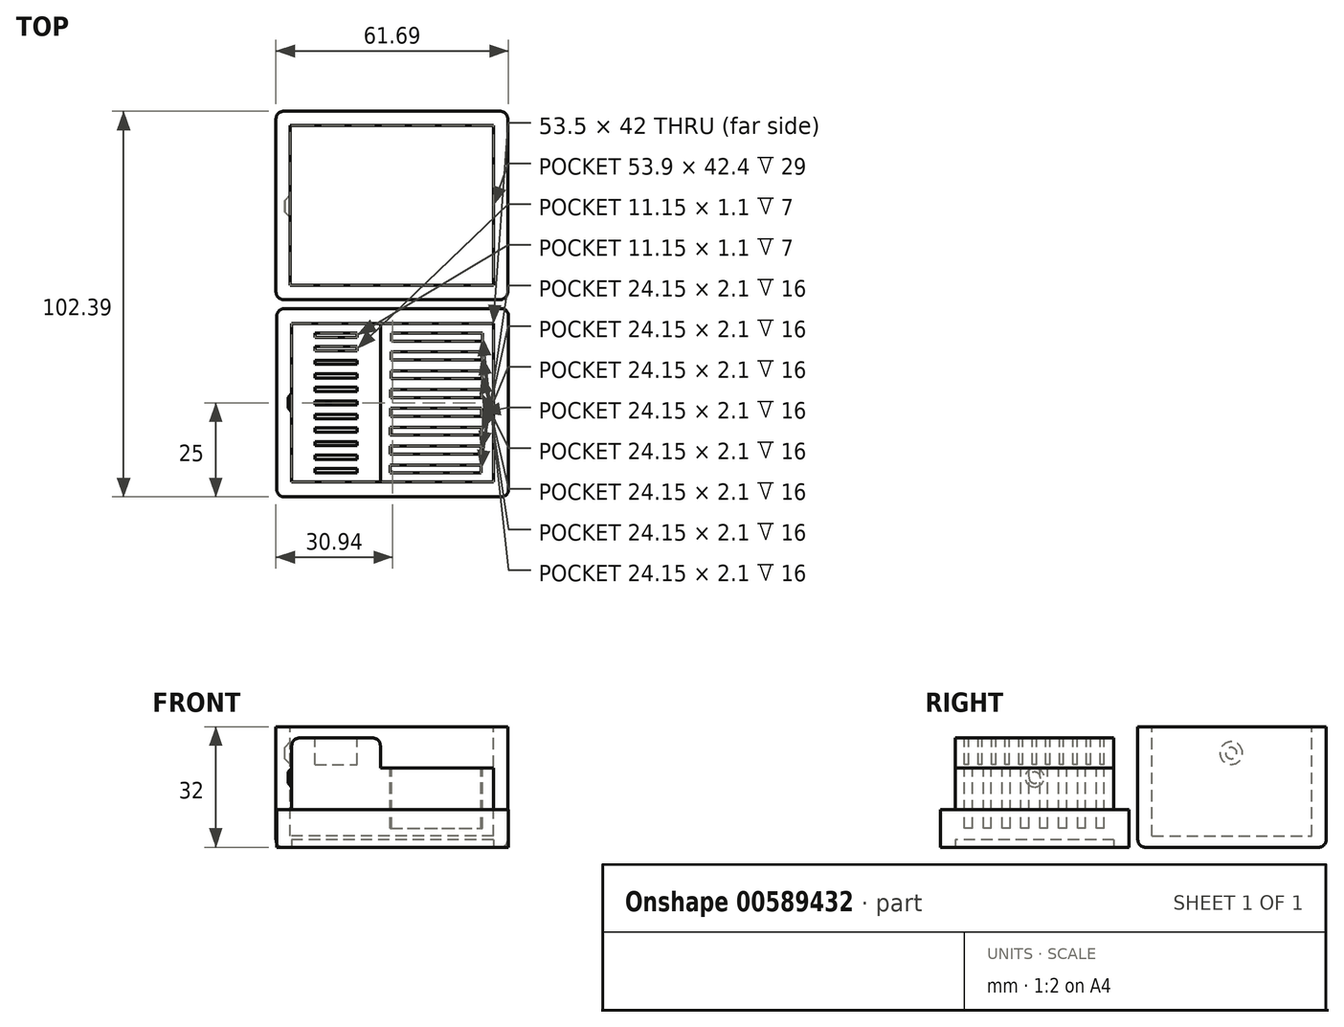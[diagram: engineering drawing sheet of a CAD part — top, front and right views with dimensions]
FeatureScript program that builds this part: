
annotation { "Feature Type Name" : "Feature", "Feature Type Description" : "" }
export const myFeature = defineFeature(function(context is Context, id is Id, definition is map)
    precondition{}
    {
        {
            var Q0;
            Q0=qCreatedBy(makeId("Top.planeOp"),FACE);
            var sketch = newSketch(context, id + "F0", { "sketchPlane" : qUnion([Q0])});
            skLineSegment(sketch, "E0.bottom", {"start": v(30.75, -25) * mm, "end": v(-30.75, -25) * mm});
            skLineSegment(sketch, "E0.top", {"start": v(30.75, 25) * mm, "end": v(-30.75, 25) * mm});
            skLineSegment(sketch, "E0.left", {"start": v(30.75, -25) * mm, "end": v(30.75, 25) * mm});
            skLineSegment(sketch, "E0.right", {"start": v(-30.75, -25) * mm, "end": v(-30.75, 25) * mm});
            skPoint(sketch, "E0.middle", {"position": v(0, 0) * mm});
            skSolve(sketch);
        }
        {
            var Q0;
            Q0=qSketchRegion(id+"F0",true);
            extrude(context, id + "F1", {"entities" : qUnion([Q0]), "depth" : 21 * mm, "offsetDistance" : 25 * mm});
        }
        {
            var Q0;
            Q0=makeQuery(id+"F1.opExtrude","CAP_FACE",FACE,{"disambiguationData":[OSD([sQuery(id+"F0.wireOp",EDGE,"E0.bottom"),sQuery(id+"F0.wireOp",EDGE,"E0.top"),sQuery(id+"F0.wireOp",EDGE,"E0.left"),sQuery(id+"F0.wireOp",EDGE,"E0.right")])],"isStart":false});
            var sketch = newSketch(context, id + "F2", { "sketchPlane" : qUnion([Q0])});
            skLineSegment(sketch, "E1.bottom", {"start": v(26.75, -21) * mm, "end": v(-26.75, -21) * mm});
            skLineSegment(sketch, "E1.top", {"start": v(26.75, 21) * mm, "end": v(-26.75, 21) * mm});
            skLineSegment(sketch, "E1.left", {"start": v(26.75, -21) * mm, "end": v(26.75, 21) * mm});
            skLineSegment(sketch, "E1.right", {"start": v(-26.75, -21) * mm, "end": v(-26.75, 21) * mm});
            skPoint(sketch, "E1.middle", {"position": v(0, 0) * mm});
            skSolve(sketch);
        }
        {
            var Q0;
            Q0=makeQuery(id+"F2.imprint","IMPRINT",FACE,{"disambiguationData":[TD([[makeQuery(id+"F2.imprint","IMPRINT",EDGE,{"derivedFrom":sQuery(id+"F2.wireOp",EDGE,"E1.bottom")}),1.0]])]});
            extrude(context, id + "F3", {"entities" : qUnion([Q0]), "operationType" : NewBodyOperationType.REMOVE, "oppositeDirection" : true, "depth" : 11 * mm, "offsetDistance" : 25 * mm});
        }
        {
            var Q0;
            Q0=makeQuery(id+"F1.opExtrude","CAP_FACE",FACE,{"disambiguationData":[OSD([sQuery(id+"F0.wireOp",EDGE,"E0.bottom"),sQuery(id+"F0.wireOp",EDGE,"E0.top"),sQuery(id+"F0.wireOp",EDGE,"E0.left"),sQuery(id+"F0.wireOp",EDGE,"E0.right")])],"isStart":false});
            var sketch = newSketch(context, id + "F4", { "sketchPlane" : qUnion([Q0])});
            skLineSegment(sketch, "E2.bottom", {"start": v(0, 21) * mm, "end": v(-26.75, 21) * mm});
            skLineSegment(sketch, "E2.top", {"start": v(0, -21) * mm, "end": v(-26.75, -21) * mm});
            skLineSegment(sketch, "E2.right", {"start": v(-26.75, 21) * mm, "end": v(-26.75, -21) * mm});
            skLineSegment(sketch, "E3.bottom", {"start": v(-26.75, 21) * mm, "end": v(-3.25, 21) * mm});
            skLineSegment(sketch, "E3.top", {"start": v(-26.75, -21) * mm, "end": v(-3.25, -21) * mm});
            skLineSegment(sketch, "E3.right", {"start": v(-3.25, 21) * mm, "end": v(-3.25, -21) * mm});
            skSolve(sketch);
        }
        {
            var Q0;
            Q0=qSketchRegion(id+"F4",true);
            extrude(context, id + "F5", {"entities" : qUnion([Q0]), "operationType" : NewBodyOperationType.ADD, "depth" : 8 * mm, "offsetDistance" : 25 * mm});
        }
        {
            var Q0;
            Q0=makeQuery(id+"F5.opExtrude","CAP_FACE",FACE,{"disambiguationData":[OSD([sQuery(id+"F4.wireOp",EDGE,"E3.bottom"),sQuery(id+"F4.wireOp",EDGE,"E3.top"),sQuery(id+"F4.wireOp",EDGE,"E2.right"),sQuery(id+"F4.wireOp",EDGE,"E3.right")])],"isStart":false});
            var sketch = newSketch(context, id + "F6", { "sketchPlane" : qUnion([Q0])});
            skLineSegment(sketch, "E4.bottom", {"start": v(-20.57, 18.5) * mm, "end": v(-9.42, 18.5) * mm});
            skLineSegment(sketch, "E4.top", {"start": v(-20.57, 17.4) * mm, "end": v(-9.42, 17.4) * mm});
            skLineSegment(sketch, "E4.left", {"start": v(-20.57, 18.5) * mm, "end": v(-20.57, 17.4) * mm});
            skLineSegment(sketch, "E4.right", {"start": v(-9.42, 18.5) * mm, "end": v(-9.42, 17.4) * mm});
            skLineSegment(sketch, "E5.1.0.0", {"start": v(-20.57, 14.9) * mm, "end": v(-9.42, 14.9) * mm});
            skLineSegment(sketch, "E5.1.0.1", {"start": v(-20.57, 13.8) * mm, "end": v(-9.42, 13.8) * mm});
            skLineSegment(sketch, "E5.1.0.2", {"start": v(-9.42, 14.9) * mm, "end": v(-9.42, 13.8) * mm});
            skLineSegment(sketch, "E5.1.0.3", {"start": v(-20.57, 14.9) * mm, "end": v(-20.57, 13.8) * mm});
            skLineSegment(sketch, "E5.2.0.0", {"start": v(-20.57, 11.3) * mm, "end": v(-9.42, 11.3) * mm});
            skLineSegment(sketch, "E5.2.0.1", {"start": v(-20.57, 10.2) * mm, "end": v(-9.42, 10.2) * mm});
            skLineSegment(sketch, "E5.2.0.2", {"start": v(-9.42, 11.3) * mm, "end": v(-9.42, 10.2) * mm});
            skLineSegment(sketch, "E5.2.0.3", {"start": v(-20.57, 11.3) * mm, "end": v(-20.57, 10.2) * mm});
            skLineSegment(sketch, "E5.3.0.0", {"start": v(-20.57, 7.7) * mm, "end": v(-9.42, 7.7) * mm});
            skLineSegment(sketch, "E5.3.0.1", {"start": v(-20.57, 6.6) * mm, "end": v(-9.42, 6.6) * mm});
            skLineSegment(sketch, "E5.3.0.2", {"start": v(-9.42, 7.7) * mm, "end": v(-9.42, 6.6) * mm});
            skLineSegment(sketch, "E5.3.0.3", {"start": v(-20.57, 7.7) * mm, "end": v(-20.57, 6.6) * mm});
            skLineSegment(sketch, "E5.4.0.0", {"start": v(-20.57, 4.1) * mm, "end": v(-9.42, 4.1) * mm});
            skLineSegment(sketch, "E5.4.0.1", {"start": v(-20.57, 3) * mm, "end": v(-9.42, 3) * mm});
            skLineSegment(sketch, "E5.4.0.2", {"start": v(-9.42, 4.1) * mm, "end": v(-9.42, 3) * mm});
            skLineSegment(sketch, "E5.4.0.3", {"start": v(-20.57, 4.1) * mm, "end": v(-20.57, 3) * mm});
            skLineSegment(sketch, "E5.5.0.0", {"start": v(-20.57, 0.5) * mm, "end": v(-9.42, 0.5) * mm});
            skLineSegment(sketch, "E5.5.0.1", {"start": v(-20.57, -0.6) * mm, "end": v(-9.42, -0.6) * mm});
            skLineSegment(sketch, "E5.5.0.2", {"start": v(-9.42, 0.5) * mm, "end": v(-9.42, -0.6) * mm});
            skLineSegment(sketch, "E5.5.0.3", {"start": v(-20.57, 0.5) * mm, "end": v(-20.57, -0.6) * mm});
            skLineSegment(sketch, "E5.6.0.0", {"start": v(-20.57, -3.1) * mm, "end": v(-9.42, -3.1) * mm});
            skLineSegment(sketch, "E5.6.0.1", {"start": v(-20.57, -4.2) * mm, "end": v(-9.42, -4.2) * mm});
            skLineSegment(sketch, "E5.6.0.2", {"start": v(-9.42, -3.1) * mm, "end": v(-9.42, -4.2) * mm});
            skLineSegment(sketch, "E5.6.0.3", {"start": v(-20.57, -3.1) * mm, "end": v(-20.57, -4.2) * mm});
            skLineSegment(sketch, "E5.7.0.0", {"start": v(-20.57, -6.7) * mm, "end": v(-9.42, -6.7) * mm});
            skLineSegment(sketch, "E5.7.0.1", {"start": v(-20.57, -7.8) * mm, "end": v(-9.42, -7.8) * mm});
            skLineSegment(sketch, "E5.7.0.2", {"start": v(-9.42, -6.7) * mm, "end": v(-9.42, -7.8) * mm});
            skLineSegment(sketch, "E5.7.0.3", {"start": v(-20.57, -6.7) * mm, "end": v(-20.57, -7.8) * mm});
            skLineSegment(sketch, "E5.8.0.0", {"start": v(-20.57, -10.3) * mm, "end": v(-9.42, -10.3) * mm});
            skLineSegment(sketch, "E5.8.0.1", {"start": v(-20.57, -11.4) * mm, "end": v(-9.42, -11.4) * mm});
            skLineSegment(sketch, "E5.8.0.2", {"start": v(-9.42, -10.3) * mm, "end": v(-9.42, -11.4) * mm});
            skLineSegment(sketch, "E5.8.0.3", {"start": v(-20.57, -10.3) * mm, "end": v(-20.57, -11.4) * mm});
            skLineSegment(sketch, "E5.9.0.0", {"start": v(-20.57, -13.9) * mm, "end": v(-9.42, -13.9) * mm});
            skLineSegment(sketch, "E5.9.0.1", {"start": v(-20.57, -15) * mm, "end": v(-9.42, -15) * mm});
            skLineSegment(sketch, "E5.9.0.2", {"start": v(-9.42, -13.9) * mm, "end": v(-9.42, -15) * mm});
            skLineSegment(sketch, "E5.9.0.3", {"start": v(-20.57, -13.9) * mm, "end": v(-20.57, -15) * mm});
            skLineSegment(sketch, "E5.10.0.0", {"start": v(-20.57, -17.5) * mm, "end": v(-9.42, -17.5) * mm});
            skLineSegment(sketch, "E5.10.0.1", {"start": v(-20.57, -18.6) * mm, "end": v(-9.42, -18.6) * mm});
            skLineSegment(sketch, "E5.10.0.2", {"start": v(-9.42, -17.5) * mm, "end": v(-9.42, -18.6) * mm});
            skLineSegment(sketch, "E5.10.0.3", {"start": v(-20.57, -17.5) * mm, "end": v(-20.57, -18.6) * mm});
            skLineSegment(sketch, "E5.direction1", {"start": v(-17.32, 17.5) * mm, "end": v(-17.32, 13.9) * mm, "construction": true});
            skSolve(sketch);
        }
        {
            var Q0;
            Q0=qSketchRegion(id+"F6",true);
            extrude(context, id + "F7", {"entities" : qUnion([Q0]), "operationType" : NewBodyOperationType.REMOVE, "oppositeDirection" : true, "depth" : 7 * mm, "offsetDistance" : 25 * mm});
        }
        {
            var Q0;
            Q0=makeQuery(id+"F1.opExtrude","CAP_FACE",FACE,{"disambiguationData":[OSD([sQuery(id+"F0.wireOp",EDGE,"E0.bottom"),sQuery(id+"F0.wireOp",EDGE,"E0.top"),sQuery(id+"F0.wireOp",EDGE,"E0.left"),sQuery(id+"F0.wireOp",EDGE,"E0.right")])],"isStart":false});
            var sketch = newSketch(context, id + "F8", { "sketchPlane" : qUnion([Q0])});
            skLineSegment(sketch, "E6.bottom", {"start": v(-0.33, 18.5) * mm, "end": v(23.82, 18.5) * mm});
            skLineSegment(sketch, "E6.top", {"start": v(-0.33, 16.4) * mm, "end": v(23.82, 16.4) * mm});
            skLineSegment(sketch, "E6.left", {"start": v(-0.33, 18.5) * mm, "end": v(-0.33, 16.4) * mm});
            skLineSegment(sketch, "E6.right", {"start": v(23.82, 18.5) * mm, "end": v(23.82, 16.4) * mm});
            skLineSegment(sketch, "E7.1.0.0", {"start": v(-0.38, 11.4) * mm, "end": v(23.77, 11.4) * mm});
            skLineSegment(sketch, "E7.1.0.1", {"start": v(23.77, 13.5) * mm, "end": v(23.77, 11.4) * mm});
            skLineSegment(sketch, "E7.1.0.2", {"start": v(-0.38, 13.5) * mm, "end": v(-0.38, 11.4) * mm});
            skLineSegment(sketch, "E7.1.0.3", {"start": v(-0.38, 13.5) * mm, "end": v(23.77, 13.5) * mm});
            skLineSegment(sketch, "E7.2.0.0", {"start": v(-0.44, 6.4) * mm, "end": v(23.71, 6.4) * mm});
            skLineSegment(sketch, "E7.2.0.1", {"start": v(23.71, 8.5) * mm, "end": v(23.71, 6.4) * mm});
            skLineSegment(sketch, "E7.2.0.2", {"start": v(-0.44, 8.5) * mm, "end": v(-0.44, 6.4) * mm});
            skLineSegment(sketch, "E7.2.0.3", {"start": v(-0.44, 8.5) * mm, "end": v(23.71, 8.5) * mm});
            skLineSegment(sketch, "E7.direction1", {"start": v(-0.33, 16.4) * mm, "end": v(-0.38, 11.4) * mm, "construction": true});
            skLineSegment(sketch, "E8.0.3.0", {"start": v(-0.5, 1.4) * mm, "end": v(23.66, 1.4) * mm});
            skLineSegment(sketch, "E8.3.3.0", {"start": v(23.66, 3.5) * mm, "end": v(23.66, 1.4) * mm});
            skLineSegment(sketch, "E8.6.3.0", {"start": v(-0.5, 3.5) * mm, "end": v(-0.5, 1.4) * mm});
            skLineSegment(sketch, "E8.9.3.0", {"start": v(-0.5, 3.5) * mm, "end": v(23.66, 3.5) * mm});
            skLineSegment(sketch, "E8.0.4.0", {"start": v(-0.55, -3.6) * mm, "end": v(23.6, -3.6) * mm});
            skLineSegment(sketch, "E8.3.4.0", {"start": v(23.6, -1.5) * mm, "end": v(23.6, -3.6) * mm});
            skLineSegment(sketch, "E8.6.4.0", {"start": v(-0.55, -1.5) * mm, "end": v(-0.55, -3.6) * mm});
            skLineSegment(sketch, "E8.9.4.0", {"start": v(-0.55, -1.5) * mm, "end": v(23.6, -1.5) * mm});
            skLineSegment(sketch, "E8.0.5.0", {"start": v(-0.6, -8.6) * mm, "end": v(23.55, -8.6) * mm});
            skLineSegment(sketch, "E8.3.5.0", {"start": v(23.55, -6.5) * mm, "end": v(23.55, -8.6) * mm});
            skLineSegment(sketch, "E8.6.5.0", {"start": v(-0.6, -6.5) * mm, "end": v(-0.6, -8.6) * mm});
            skLineSegment(sketch, "E8.9.5.0", {"start": v(-0.6, -6.5) * mm, "end": v(23.55, -6.5) * mm});
            skLineSegment(sketch, "E9.0.6.0", {"start": v(-0.66, -13.6) * mm, "end": v(23.5, -13.6) * mm});
            skLineSegment(sketch, "E9.3.6.0", {"start": v(23.5, -11.5) * mm, "end": v(23.5, -13.6) * mm});
            skLineSegment(sketch, "E9.6.6.0", {"start": v(-0.66, -11.5) * mm, "end": v(-0.66, -13.6) * mm});
            skLineSegment(sketch, "E9.9.6.0", {"start": v(-0.66, -11.5) * mm, "end": v(23.5, -11.5) * mm});
            skLineSegment(sketch, "E10.0.7.0", {"start": v(-0.71, -18.6) * mm, "end": v(23.44, -18.6) * mm});
            skLineSegment(sketch, "E10.3.7.0", {"start": v(23.44, -16.5) * mm, "end": v(23.44, -18.6) * mm});
            skLineSegment(sketch, "E10.6.7.0", {"start": v(-0.71, -16.5) * mm, "end": v(-0.71, -18.6) * mm});
            skLineSegment(sketch, "E10.9.7.0", {"start": v(-0.71, -16.5) * mm, "end": v(23.44, -16.5) * mm});
            skSolve(sketch);
        }
        {
            var Q0;
            Q0=qSketchRegion(id+"F8",true);
            extrude(context, id + "F9", {"entities" : qUnion([Q0]), "operationType" : NewBodyOperationType.REMOVE, "oppositeDirection" : true, "depth" : 16 * mm, "offsetDistance" : 25 * mm});
        }
        {
            var Q0;
            Q0=makeQuery(id+"F5.opExtrude","CAP_EDGE",EDGE,{"disambiguationData":[OSD([sQuery(id+"F4.wireOp",EDGE,"E3.right")])],"isStart":false});
            var Q1;
            Q1=makeQuery(id+"F3.boolean.opBoolean","COPY",EDGE,{"derivedFrom":makeQuery(id+"F3.opExtrude","CAP_EDGE",EDGE,{"disambiguationData":[OSD([sQuery(id+"F2.wireOp",EDGE,"E1.left")])],"isStart":true})});
            var Q2;
            Q2=makeQuery(id+"F5.opExtrude","CAP_EDGE",EDGE,{"disambiguationData":[OSD([sQuery(id+"F4.wireOp",EDGE,"E2.right")])],"isStart":false});
            var Q3;
            Q3=makeQuery(id+"F5.opExtrude","CAP_EDGE",EDGE,{"disambiguationData":[OSD([sQuery(id+"F4.wireOp",EDGE,"E3.right")])],"isStart":true});
            var Q4;
            Q4=makeQuery(id+"F1.opExtrude","SWEPT_EDGE",EDGE,{"disambiguationData":[OSD([sQuery(id+"F0.wireOp",EDGE,"E0.bottom"),sQuery(id+"F0.wireOp",EDGE,"E0.right")])]});
            var Q5;
            Q5=makeQuery(id+"F1.opExtrude","SWEPT_EDGE",EDGE,{"disambiguationData":[OSD([sQuery(id+"F0.wireOp",EDGE,"E0.top"),sQuery(id+"F0.wireOp",EDGE,"E0.right")])]});
            var Q6;
            Q6=makeQuery(id+"F1.opExtrude","SWEPT_EDGE",EDGE,{"disambiguationData":[OSD([sQuery(id+"F0.wireOp",EDGE,"E0.bottom"),sQuery(id+"F0.wireOp",EDGE,"E0.left")])]});
            var Q7;
            Q7=makeQuery(id+"F1.opExtrude","SWEPT_EDGE",EDGE,{"disambiguationData":[OSD([sQuery(id+"F0.wireOp",EDGE,"E0.top"),sQuery(id+"F0.wireOp",EDGE,"E0.left")])]});
            var Q8;
            Q8=makeQuery(id+"F5.opExtrude","CAP_EDGE",EDGE,{"disambiguationData":[OSD([sQuery(id+"F4.wireOp",EDGE,"E3.top")])],"isStart":false});
            var Q9;
            Q9=makeQuery(id+"F3.boolean.opBoolean","COPY",EDGE,{"derivedFrom":makeQuery(id+"F3.opExtrude","CAP_EDGE",EDGE,{"disambiguationData":[OSD([sQuery(id+"F2.wireOp",EDGE,"E1.bottom")])],"isStart":true})});
            var Q10;
            Q10=makeQuery(id+"F3.boolean.opBoolean","COPY",EDGE,{"derivedFrom":makeQuery(id+"F3.opExtrude","CAP_EDGE",EDGE,{"disambiguationData":[OSD([sQuery(id+"F2.wireOp",EDGE,"E1.top")])],"isStart":true})});
            var Q11;
            Q11=makeQuery(id+"F5.opExtrude","CAP_EDGE",EDGE,{"disambiguationData":[OSD([sQuery(id+"F4.wireOp",EDGE,"E3.bottom")])],"isStart":false});
            fillet(context, id + "F10", {"entities" : qUnion([Q0, Q1, Q2, Q3, Q4, Q5, Q6, Q7, Q8, Q9, Q10, Q11]), "radius" : 2 * mm, "tangentPropagation" : true, "allowEdgeOverflow" : false});
        }
        {
            var Q0;
            Q0=qCreatedBy(makeId("Top.planeOp"),FACE);
            var sketch = newSketch(context, id + "F11", { "sketchPlane" : qUnion([Q0])});
            skLineSegment(sketch, "E11.bottom", {"start": v(-30.94, 77.39) * mm, "end": v(30.56, 77.39) * mm});
            skLineSegment(sketch, "E11.top", {"start": v(-30.94, 27.39) * mm, "end": v(30.56, 27.39) * mm});
            skLineSegment(sketch, "E11.left", {"start": v(-30.94, 77.39) * mm, "end": v(-30.94, 27.39) * mm});
            skLineSegment(sketch, "E11.right", {"start": v(30.56, 77.39) * mm, "end": v(30.56, 27.39) * mm});
            skSolve(sketch);
        }
        {
            var Q0;
            Q0=qSketchRegion(id+"F11",true);
            extrude(context, id + "F12", {"entities" : qUnion([Q0]), "depth" : 32 * mm, "offsetDistance" : 25 * mm});
        }
        {
            var Q0;
            Q0=makeQuery(id+"F12.opExtrude","CAP_FACE",FACE,{"disambiguationData":[OSD([sQuery(id+"F11.wireOp",EDGE,"E11.bottom"),sQuery(id+"F11.wireOp",EDGE,"E11.top"),sQuery(id+"F11.wireOp",EDGE,"E11.left"),sQuery(id+"F11.wireOp",EDGE,"E11.right")])],"isStart":false});
            var sketch = newSketch(context, id + "F13", { "sketchPlane" : qUnion([Q0])});
            skLineSegment(sketch, "E12.bottom", {"start": v(26.76, 31.19) * mm, "end": v(-27.14, 31.19) * mm});
            skLineSegment(sketch, "E12.top", {"start": v(26.76, 73.59) * mm, "end": v(-27.14, 73.59) * mm});
            skLineSegment(sketch, "E12.left", {"start": v(26.76, 31.19) * mm, "end": v(26.76, 73.59) * mm});
            skLineSegment(sketch, "E12.right", {"start": v(-27.14, 31.19) * mm, "end": v(-27.14, 73.59) * mm});
            skPoint(sketch, "E12.middle", {"position": v(-0.2, 52.39) * mm});
            skPoint(sketch, "E12.middle.positionSnap0", {"position": v(-30.94, 52.39) * mm});
            skPoint(sketch, "E12.middle.positionSnap1", {"position": v(-0.2, 77.39) * mm});
            skPoint(sketch, "E12.centerSnap0", {"position": v(-30.94, 52.39) * mm});
            skPoint(sketch, "E12.centerSnap1", {"position": v(-0.2, 77.39) * mm});
            skSolve(sketch);
        }
        {
            var Q0;
            Q0=qSketchRegion(id+"F13",true);
            extrude(context, id + "F14", {"entities" : qUnion([Q0]), "operationType" : NewBodyOperationType.REMOVE, "oppositeDirection" : true, "depth" : 29 * mm, "offsetDistance" : 25 * mm});
        }
        {
            var Q0;
            Q0=makeQuery(id+"F5.boolean.opBoolean","MERGE",FACE,{"derivedFrom":[makeQuery(id+"F3.boolean.opBoolean","COPY",FACE,{"derivedFrom":makeQuery(id+"F3.opExtrude","SWEPT_FACE",FACE,{"disambiguationData":[OSD([sQuery(id+"F2.wireOp",EDGE,"E1.right")])]})}),makeQuery(id+"F5.opExtrude","SWEPT_FACE",FACE,{"disambiguationData":[OSD([sQuery(id+"F4.wireOp",EDGE,"E2.right")])]})]});
            var sketch = newSketch(context, id + "F15", { "sketchPlane" : qUnion([Q0])});
            skCircle(sketch, "E13", {"center": v(0, 18.5) * mm, "radius": 2.5 * mm});
            skPoint(sketch, "E13.centerSnap0", {"position": v(-21, 18.5) * mm});
            skPoint(sketch, "E13.centerSnap1", {"position": v(0, 27) * mm});
            skSolve(sketch);
        }
        {
            var Q0;
            Q0=qSketchRegion(id+"F15",true);
            extrude(context, id + "F16", {"entities" : qUnion([Q0]), "operationType" : NewBodyOperationType.ADD, "depth" : 1 * mm, "offsetDistance" : 25 * mm, "hasDraft" : true, "draftAngle" : 45 * degree, "draftPullDirection" : true});
        }
        {
            var Q0;
            Q0=makeQuery(id+"F14.boolean.opBoolean","COPY",FACE,{"derivedFrom":makeQuery(id+"F14.opExtrude","SWEPT_FACE",FACE,{"disambiguationData":[OSD([sQuery(id+"F13.wireOp",EDGE,"E12.right")])]})});
            var sketch = newSketch(context, id + "F17", { "sketchPlane" : qUnion([Q0])});
            skCircle(sketch, "E14", {"center": v(52.19, 25) * mm, "radius": 3 * mm});
            skSolve(sketch);
        }
        {
            var Q0;
            Q0=qSketchRegion(id+"F17",true);
            extrude(context, id + "F18", {"entities" : qUnion([Q0]), "operationType" : NewBodyOperationType.REMOVE, "oppositeDirection" : true, "depth" : 1.5 * mm, "offsetDistance" : 25 * mm, "hasDraft" : true, "draftAngle" : 45 * degree, "draftPullDirection" : true});
        }
        {
            var Q0;
            Q0=makeQuery(id+"F12.opExtrude","CAP_FACE",FACE,{"disambiguationData":[OSD([sQuery(id+"F11.wireOp",EDGE,"E11.bottom"),sQuery(id+"F11.wireOp",EDGE,"E11.top"),sQuery(id+"F11.wireOp",EDGE,"E11.left"),sQuery(id+"F11.wireOp",EDGE,"E11.right")])],"isStart":true});
            var Q1;
            Q1=makeQuery(id+"F12.opExtrude","SWEPT_EDGE",EDGE,{"disambiguationData":[OSD([sQuery(id+"F11.wireOp",EDGE,"E11.bottom"),sQuery(id+"F11.wireOp",EDGE,"E11.left")])]});
            var Q2;
            Q2=makeQuery(id+"F12.opExtrude","SWEPT_EDGE",EDGE,{"disambiguationData":[OSD([sQuery(id+"F11.wireOp",EDGE,"E11.top"),sQuery(id+"F11.wireOp",EDGE,"E11.left")])]});
            var Q3;
            Q3=makeQuery(id+"F12.opExtrude","SWEPT_EDGE",EDGE,{"disambiguationData":[OSD([sQuery(id+"F11.wireOp",EDGE,"E11.top"),sQuery(id+"F11.wireOp",EDGE,"E11.right")])]});
            var Q4;
            Q4=makeQuery(id+"F12.opExtrude","SWEPT_EDGE",EDGE,{"disambiguationData":[OSD([sQuery(id+"F11.wireOp",EDGE,"E11.bottom"),sQuery(id+"F11.wireOp",EDGE,"E11.right")])]});
            fillet(context, id + "F19", {"entities" : qUnion([Q0, Q1, Q2, Q3, Q4]), "radius" : 2 * mm, "tangentPropagation" : true, "allowEdgeOverflow" : false});
        }
        {
            var Q0;
            Q0=makeQuery(id+"F1.opExtrude","CAP_FACE",FACE,{"disambiguationData":[OSD([sQuery(id+"F0.wireOp",EDGE,"E0.bottom"),sQuery(id+"F0.wireOp",EDGE,"E0.top"),sQuery(id+"F0.wireOp",EDGE,"E0.left"),sQuery(id+"F0.wireOp",EDGE,"E0.right")])],"isStart":true});
            var sketch = newSketch(context, id + "F20", { "sketchPlane" : qUnion([Q0])});
            skLineSegment(sketch, "E15.bottom", {"start": v(26.75, -21) * mm, "end": v(-26.75, -21) * mm});
            skLineSegment(sketch, "E15.top", {"start": v(26.75, 21) * mm, "end": v(-26.75, 21) * mm});
            skLineSegment(sketch, "E15.left", {"start": v(26.75, -21) * mm, "end": v(26.75, 21) * mm});
            skLineSegment(sketch, "E15.right", {"start": v(-26.75, -21) * mm, "end": v(-26.75, 21) * mm});
            skPoint(sketch, "E15.middle", {"position": v(0, 0) * mm});
            skSolve(sketch);
        }
        {
            var Q0;
            Q0=makeQuery(id+"F20.imprint","IMPRINT",FACE,{"disambiguationData":[TD([[makeQuery(id+"F20.imprint","IMPRINT",EDGE,{"derivedFrom":sQuery(id+"F20.wireOp",EDGE,"E15.bottom")}),-1.0]])]});
            extrude(context, id + "F21", {"entities" : qUnion([Q0]), "operationType" : NewBodyOperationType.REMOVE, "oppositeDirection" : true, "depth" : 2 * mm, "offsetDistance" : 25 * mm});
        }
    });
